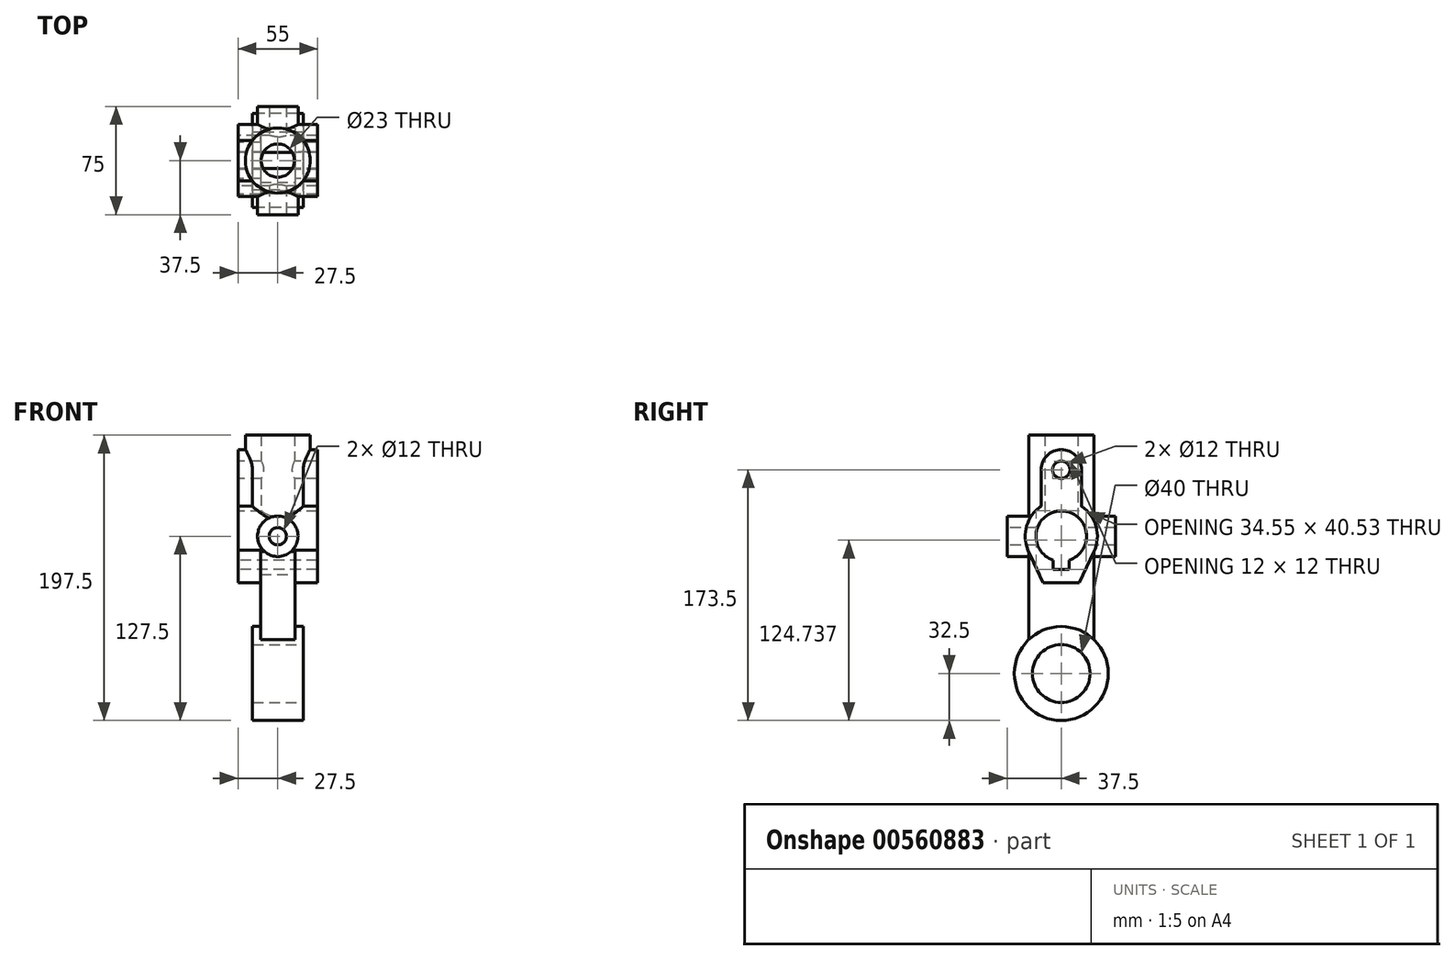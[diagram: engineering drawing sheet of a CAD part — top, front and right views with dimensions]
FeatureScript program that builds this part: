
annotation { "Feature Type Name" : "Feature", "Feature Type Description" : "" }
export const myFeature = defineFeature(function(context is Context, id is Id, definition is map)
    precondition{}
    {
        {
            var Q0;
            Q0=qCreatedBy(makeId("Top.planeOp"),FACE);
            var sketch = newSketch(context, id + "F0", { "sketchPlane" : qUnion([Q0])});
            skCircle(sketch, "E0", {"center": v(0, 0) * mm, "radius": 22.5 * mm});
            skCircle(sketch, "E1", {"center": v(0, 0) * mm, "radius": 11.5 * mm});
            skSolve(sketch);
        }
        {
            var Q0;
            Q0 = qSketchRegion(id + "F0", true);
            extrude(context, id + "F1", {"entities" : qUnion([Q0]), "depth" : 70 * mm, "offsetDistance" : 25 * mm});
        }
        {
            var Q0;
            Q0=qCreatedBy(makeId("Right.planeOp"),FACE);
            var sketch = newSketch(context, id + "F2", { "sketchPlane" : qUnion([Q0])});
            skArc(sketch, "E2", {"start": v(5.5, -16.61) * mm, "mid": v(0, 17.5) * mm, "end": v(-5.5, -16.61) * mm});
            skLineSegment(sketch, "E3", {"start": v(0, -23.03) * mm, "end": v(-5.5, -23.03) * mm});
            skLineSegment(sketch, "E4", {"start": v(0, -23.03) * mm, "end": v(5.5, -23.03) * mm});
            skLineSegment(sketch, "E5", {"start": v(5.5, -23.03) * mm, "end": v(5.5, -16.61) * mm});
            skLineSegment(sketch, "E6", {"start": v(-5.5, -23.03) * mm, "end": v(-5.5, -16.61) * mm});
            skLineSegment(sketch, "E7", {"start": v(0, -23.03) * mm, "end": v(0, -32.03) * mm});
            skLineSegment(sketch, "E8", {"start": v(0, -32.03) * mm, "end": v(-12.5, -32.03) * mm});
            skLineSegment(sketch, "E9", {"start": v(0, -32.03) * mm, "end": v(12.5, -32.03) * mm});
            skLineSegment(sketch, "E10", {"start": v(12.5, -32.03) * mm, "end": v(22.6, -10.7) * mm});
            skLineSegment(sketch, "E11", {"start": v(-12.5, -32.03) * mm, "end": v(-23.12, -9.5) * mm});
            skPoint(sketch, "E12.orphan", {"position": v(-27.6, 0) * mm});
            skPoint(sketch, "E13.end.orphan", {"position": v(12.5, 43.8) * mm});
            skPoint(sketch, "E14.orphan", {"position": v(-13.88, 43.8) * mm});
            skPoint(sketch, "E15.end.orphan", {"position": v(0, 23) * mm});
            skPoint(sketch, "E16.trimOffspring.end.orphan", {"position": v(-15.87, 23) * mm});
            skArc(sketch, "E17", {"start": v(22.6, -10.7) * mm, "mid": v(24.11, 6.6) * mm, "end": v(14, 20.71) * mm});
            skLineSegment(sketch, "E18", {"start": v(0, 40) * mm, "end": v(0, 46) * mm});
            skArc(sketch, "E19", {"start": v(14, 46) * mm, "mid": v(0, 60) * mm, "end": v(-14, 46) * mm});
            skCircle(sketch, "E20", {"center": v(0, 46) * mm, "radius": 6 * mm});
            skLineSegment(sketch, "E21", {"start": v(14, 46) * mm, "end": v(14, 20.71) * mm});
            skLineSegment(sketch, "E22", {"start": v(-14, 46) * mm, "end": v(-14, 20.71) * mm});
            skArc(sketch, "E23.trimOffspring", {"start": v(-14, 20.71) * mm, "mid": v(-23.93, 7.23) * mm, "end": v(-23.12, -9.5) * mm});
            skLineSegment(sketch, "E24", {"start": v(0, -32.03) * mm, "end": v(0, 0) * mm});
            skSolve(sketch);
        }
        {
            var Q0;
            Q0 = qSketchRegion(id + "F2", true);
            extrude(context, id + "F3", {"entities" : qUnion([Q0]), "operationType" : NewBodyOperationType.ADD, "endBound" : BoundingType.SYMMETRIC, "depth" : 55 * mm, "offsetDistance" : 25 * mm});
        }
        {
            var Q0;
            Q0=qCreatedBy(makeId("Front.planeOp"),FACE);
            var sketch = newSketch(context, id + "F4", { "sketchPlane" : qUnion([Q0])});
            skCircle(sketch, "E25", {"center": v(0, 0) * mm, "radius": 6 * mm});
            skSolve(sketch);
        }
        {
            var Q0;
            Q0 = qSketchRegion(id + "F4", true);
            extrude(context, id + "F5", {"entities" : qUnion([Q0]), "operationType" : NewBodyOperationType.REMOVE, "endBound" : BoundingType.THROUGH_ALL, "oppositeDirection" : true, "depth" : 25 * mm, "offsetDistance" : 25 * mm});
        }
        {
            var Q0;
            Q0 = qSketchRegion(id + "F4", true);
            extrude(context, id + "F6", {"entities" : qUnion([Q0]), "operationType" : NewBodyOperationType.REMOVE, "depth" : 25 * mm, "offsetDistance" : 25 * mm});
        }
        {
            var Q0;
            Q0=qCreatedBy(makeId("Front.planeOp"),FACE);
            var sketch = newSketch(context, id + "F7", { "sketchPlane" : qUnion([Q0])});
            skCircle(sketch, "E26", {"center": v(0, 0) * mm, "radius": 14 * mm});
            skCircle(sketch, "E27", {"center": v(0, 0) * mm, "radius": 6 * mm});
            skSolve(sketch);
        }
        {
            var Q0;
            Q0 = qSketchRegion(id + "F7", true);
            extrude(context, id + "F8", {"entities" : qUnion([Q0]), "operationType" : NewBodyOperationType.ADD, "endBound" : BoundingType.SYMMETRIC, "depth" : 75 * mm, "offsetDistance" : 25 * mm});
        }
        {
            var Q0;
            Q0=qCreatedBy(makeId("Right.planeOp"),FACE);
            var sketch = newSketch(context, id + "F9", { "sketchPlane" : qUnion([Q0])});
            skArc(sketch, "E28", {"start": v(5.5, -16.61) * mm, "mid": v(0, 17.5) * mm, "end": v(-5.5, -16.61) * mm});
            skLineSegment(sketch, "E29", {"start": v(0, -23) * mm, "end": v(5.5, -23) * mm});
            skLineSegment(sketch, "E30", {"start": v(0, -23) * mm, "end": v(-5.5, -23) * mm});
            skLineSegment(sketch, "E31", {"start": v(-5.5, -23) * mm, "end": v(-5.5, -16.61) * mm});
            skLineSegment(sketch, "E32", {"start": v(5.5, -23) * mm, "end": v(5.5, -16.61) * mm});
            skCircle(sketch, "E33", {"center": v(0, 46) * mm, "radius": 6 * mm});
            skSolve(sketch);
        }
        {
            var Q0;
            Q0 = qSketchRegion(id + "F9", true);
            extrude(context, id + "F10", {"entities" : qUnion([Q0]), "operationType" : NewBodyOperationType.REMOVE, "endBound" : BoundingType.THROUGH_ALL, "oppositeDirection" : true, "depth" : 25 * mm, "offsetDistance" : 25 * mm});
        }
        {
            var Q0;
            Q0 = qSketchRegion(id + "F9", true);
            extrude(context, id + "F11", {"entities" : qUnion([Q0]), "operationType" : NewBodyOperationType.REMOVE, "depth" : 25 * mm, "offsetDistance" : 25 * mm});
        }
        {
            var Q0;
            Q0=qCreatedBy(makeId("Right.planeOp"),FACE);
            var sketch = newSketch(context, id + "F12", { "sketchPlane" : qUnion([Q0])});
            skArc(sketch, "E34", {"start": v(22.6, -10.7) * mm, "mid": v(0, 25) * mm, "end": v(-22.6, -10.7) * mm});
            skLineSegment(sketch, "E35", {"start": v(0, -32) * mm, "end": v(12.5, -32) * mm});
            skLineSegment(sketch, "E36", {"start": v(12.5, -32) * mm, "end": v(-12.5, -32) * mm});
            skLineSegment(sketch, "E37", {"start": v(-12.5, -32) * mm, "end": v(-22.6, -10.7) * mm});
            skLineSegment(sketch, "E38", {"start": v(12.5, -32) * mm, "end": v(22.6, -10.7) * mm});
            skArc(sketch, "E39", {"start": v(5.5, -16.61) * mm, "mid": v(0, 17.5) * mm, "end": v(-5.5, -16.61) * mm});
            skLineSegment(sketch, "E40", {"start": v(0, -23) * mm, "end": v(-5.5, -23) * mm});
            skLineSegment(sketch, "E41", {"start": v(-5.5, -23) * mm, "end": v(5.5, -23) * mm});
            skLineSegment(sketch, "E42", {"start": v(5.5, -23) * mm, "end": v(5.5, -16.61) * mm});
            skLineSegment(sketch, "E43", {"start": v(-5.5, -23) * mm, "end": v(-5.5, -16.61) * mm});
            skLineSegment(sketch, "E44", {"start": v(0, 0) * mm, "end": v(0, -14) * mm});
            skLineSegment(sketch, "E45", {"start": v(0, -14) * mm, "end": v(90.3, -14) * mm});
            skLineSegment(sketch, "E46", {"start": v(0, -14) * mm, "end": v(-68.22, -14) * mm});
            skLineSegment(sketch, "E47", {"start": v(0, 0) * mm, "end": v(0, -95) * mm});
            skLineSegment(sketch, "E48", {"start": v(0, -95) * mm, "end": v(-22.5, -95) * mm});
            skLineSegment(sketch, "E49", {"start": v(-22.5, -95) * mm, "end": v(22.5, -95) * mm});
            skLineSegment(sketch, "E50", {"start": v(-22.5, -95) * mm, "end": v(-22.6, -10.7) * mm});
            skPoint(sketch, "E51.end.orphan", {"position": v(21.03, -95) * mm});
            skPoint(sketch, "E52.end.orphan", {"position": v(22.5, -14) * mm});
            skLineSegment(sketch, "E53", {"start": v(22.5, -95) * mm, "end": v(22.6, -10.7) * mm});
            skSolve(sketch);
        }
        {
            var Q0;
            Q0 = qSketchRegion(id + "F12", true);
            extrude(context, id + "F13", {"entities" : qUnion([Q0]), "operationType" : NewBodyOperationType.ADD, "endBound" : BoundingType.SYMMETRIC, "depth" : 24 * mm, "offsetDistance" : 25 * mm});
        }
        {
            var Q0;
            Q0=qCreatedBy(makeId("Right.planeOp"),FACE);
            var sketch = newSketch(context, id + "F14", { "sketchPlane" : qUnion([Q0])});
            skLineSegment(sketch, "E54", {"start": v(0, 0) * mm, "end": v(0, -95) * mm});
            skCircle(sketch, "E55", {"center": v(0, -95) * mm, "radius": 32.5 * mm});
            skSolve(sketch);
        }
        {
            var Q0;
            Q0 = qSketchRegion(id + "F14", true);
            extrude(context, id + "F15", {"entities" : qUnion([Q0]), "operationType" : NewBodyOperationType.ADD, "endBound" : BoundingType.SYMMETRIC, "depth" : 35 * mm, "offsetDistance" : 25 * mm});
        }
        {
            var Q0;
            Q0=makeQuery(id+"F15.opExtrude","CAP_FACE",FACE,{"disambiguationData":[OSD([sQuery(id+"F14.wireOp",EDGE,"E55")])],"isStart":false});
            var sketch = newSketch(context, id + "F16", { "sketchPlane" : qUnion([Q0])});
            skLineSegment(sketch, "E56", {"start": v(0, 0) * mm, "end": v(0, -95) * mm});
            skCircle(sketch, "E57", {"center": v(0, -95) * mm, "radius": 20 * mm});
            skSolve(sketch);
        }
        {
            var Q0;
            Q0 = qSketchRegion(id + "F16", true);
            extrude(context, id + "F17", {"entities" : qUnion([Q0]), "operationType" : NewBodyOperationType.REMOVE, "endBound" : BoundingType.THROUGH_ALL, "oppositeDirection" : true, "depth" : 40 * mm, "offsetDistance" : 25 * mm});
        }
        {
            var Q0;
            Q0=makeQuery(id+"F8.opExtrude","CAP_FACE",FACE,{"disambiguationData":[OSD([sQuery(id+"F7.wireOp",EDGE,"E26"),sQuery(id+"F7.wireOp",EDGE,"E27")])],"isStart":true});
            var sketch = newSketch(context, id + "F18", { "sketchPlane" : qUnion([Q0])});
            skCircle(sketch, "E58", {"center": v(0, 0) * mm, "radius": 6 * mm});
            skSolve(sketch);
        }
        {
            var Q0;
            Q0 = qSketchRegion(id + "F18", true);
            extrude(context, id + "F19", {"entities" : qUnion([Q0]), "operationType" : NewBodyOperationType.REMOVE, "endBound" : BoundingType.THROUGH_ALL, "oppositeDirection" : true, "depth" : 25 * mm, "offsetDistance" : 25 * mm});
        }
        {
            var Q0;
            Q0=makeQuery(id+"F1.opExtrude","CAP_FACE",FACE,{"disambiguationData":[OSD([sQuery(id+"F0.wireOp",EDGE,"E0"),sQuery(id+"F0.wireOp",EDGE,"E1")])],"isStart":false});
            var sketch = newSketch(context, id + "F20", { "sketchPlane" : qUnion([Q0])});
            skCircle(sketch, "E59", {"center": v(0, 0) * mm, "radius": 11.5 * mm});
            skSolve(sketch);
        }
        {
            var Q0;
            Q0 = qSketchRegion(id + "F20", true);
            extrude(context, id + "F21", {"entities" : qUnion([Q0]), "operationType" : NewBodyOperationType.REMOVE, "oppositeDirection" : true, "depth" : 70 * mm, "offsetDistance" : 25 * mm});
        }
    });
